# Revit family: Skyfull_Porta-Pivotante-35
name_source: partatom
category: Doors
units: mm (PartAtom-declared; Revit-internal decimal feet)

## family parameters
Always vertical = Yes
Cut with Voids When Loaded = No
Host = Wall
OmniClass Number = 23.30.10.00
OmniClass Title = Doors
Room Calculation Point = No
Shared = No

## types (12) — shared parameters
Altura Maçaneta = 110 cm
Analytic Construction = <Nenhum>
Define Thermal Properties by = Schematic Type
Description = Porta pivotante com esquadria minimalista de alumínio e vidro, 1 Folha
Deslocamento Pivô = 24 cm
Developer = Blocks
Espessura‎ ‎ = 1 cm
Externo = Yes
Instalação = A partir da face interna da parede
Interno = Yes
Largura‎ ‎ = 5 cm
Manufacturer = Ulimax&Co
Maçaneta = Yes
Pivô = Entre 15% e 50% da largura do vão
Thickness = 7 cm
Type Comments = Porta Pivotante Skyfull
URL = https://www.ulimax.com.br
URL Developer = https://BlocksRvt.com
URL Produto = https://www.skyfull.com.br
URL Template = https://www.skyfull.com.br
Visor = Skyfull - Glass - Transparent
Wall Closure = By host
b = 24.8 cm
zero-valued in all types: Deslocamento Instalação‎ ‎

## per-type parameters (varying)
| type | Alizar | Batente | Caixilho | Height | Puxador | Rough Height | Rough Width | Width |
| Branco - 1.20 x  2.40 | Skyfull - Metal - Beige - Matte - 230-200-160 | Skyfull - Metal - Beige - Matte - 230-200-160 | Skyfull - Metal - Beige - Matte - 230-200-160 | 240 cm | Skyfull - Metal - Beige - Matte - 230-200-160 | 240 cm | 121.6 cm | 120 cm |
| Cinza - 0.80 x 2.10 | Skyfull - Metal - Chrome - 203-203-203 | Skyfull - Metal - Chrome - 203-203-203 | Skyfull - Metal - Chrome - 203-203-203 | 210 cm | Skyfull - Metal - Chrome - 203-203-203 | 210 cm | 81.6 cm | 80 cm |
| Branco - 1.00 x 2.10 | Skyfull - Metal - White - Matte - 246-246-243 | Skyfull - Metal - White - Matte - 246-246-243 | Skyfull - Metal - White - Matte - 246-246-243 | 210 cm | Skyfull - Metal - White - Matte - 246-246-243 | 210 cm | 101.6 cm | 100 cm |
| Preto - 0.80 x 2.10 | Skyfull - Metal - Black - Matte - 15-15-15 | Skyfull - Metal - Black - Matte - 15-15-15 | Skyfull - Metal - Black - Matte - 15-15-15 | 210 cm | Skyfull - Metal - Black - Matte - 15-15-15 | 210 cm | 81.6 cm | 80 cm |
| Preto - 1.00 x 2.10 | Skyfull - Metal - Black - Matte - 15-15-15 | Skyfull - Metal - Black - Matte - 15-15-15 | Skyfull - Metal - Black - Matte - 15-15-15 | 210 cm | Skyfull - Metal - Black - Matte - 15-15-15 | 210 cm | 101.6 cm | 100 cm |
| Branco - 0.80 x 2.10 | Skyfull - Metal - White - Matte - 246-246-243 | Skyfull - Metal - White - Matte - 246-246-243 | Skyfull - Metal - White - Matte - 246-246-243 | 210 cm | Skyfull - Metal - White - Matte - 246-246-243 | 210 cm | 81.6 cm | 80 cm |
| Champanhe - 1.20 x 2.40 | Skyfull - Metal - Beige - Matte - 230-200-160 | Skyfull - Metal - Beige - Matte - 230-200-160 | Skyfull - Metal - Beige - Matte - 230-200-160 | 240 cm | Skyfull - Metal - Beige - Matte - 230-200-160 | 240 cm | 121.6 cm | 120 cm |
| Champanhe - 0.80 x 2.10 | Skyfull - Metal - Beige - Matte - 230-200-160 | Skyfull - Metal - Beige - Matte - 230-200-160 | Skyfull - Metal - Beige - Matte - 230-200-160 | 210 cm | Skyfull - Metal - Beige - Matte - 230-200-160 | 210 cm | 81.6 cm | 80 cm |
| Champanhe - 1.00 x 2.10 | Skyfull - Metal - Beige - Matte - 230-200-160 | Skyfull - Metal - Beige - Matte - 230-200-160 | Skyfull - Metal - Beige - Matte - 230-200-160 | 210 cm | Skyfull - Metal - Beige - Matte - 230-200-160 | 210 cm | 101.6 cm | 100 cm |
| Cinza - 1.00 x 2.10 | Skyfull - Metal - Chrome - 203-203-203 | Skyfull - Metal - Chrome - 203-203-203 | Skyfull - Metal - Chrome - 203-203-203 | 210 cm | Skyfull - Metal - Chrome - 203-203-203 | 210 cm | 101.6 cm | 100 cm |
| Cinza - 1.20 x 2.40 | Skyfull - Metal - Chrome - 203-203-203 | Skyfull - Metal - Chrome - 203-203-203 | Skyfull - Metal - Chrome - 203-203-203 | 240 cm | Skyfull - Metal - Chrome - 203-203-203 | 240 cm | 121.6 cm | 120 cm |
| Preto - 1.20 x 2.40 | Skyfull - Metal - Black - Matte - 15-15-15 | Skyfull - Metal - Black - Matte - 15-15-15 | Skyfull - Metal - Black - Matte - 15-15-15 | 240 cm | Skyfull - Metal - Black - Matte - 15-15-15 | 240 cm | 121.6 cm | 120 cm |
